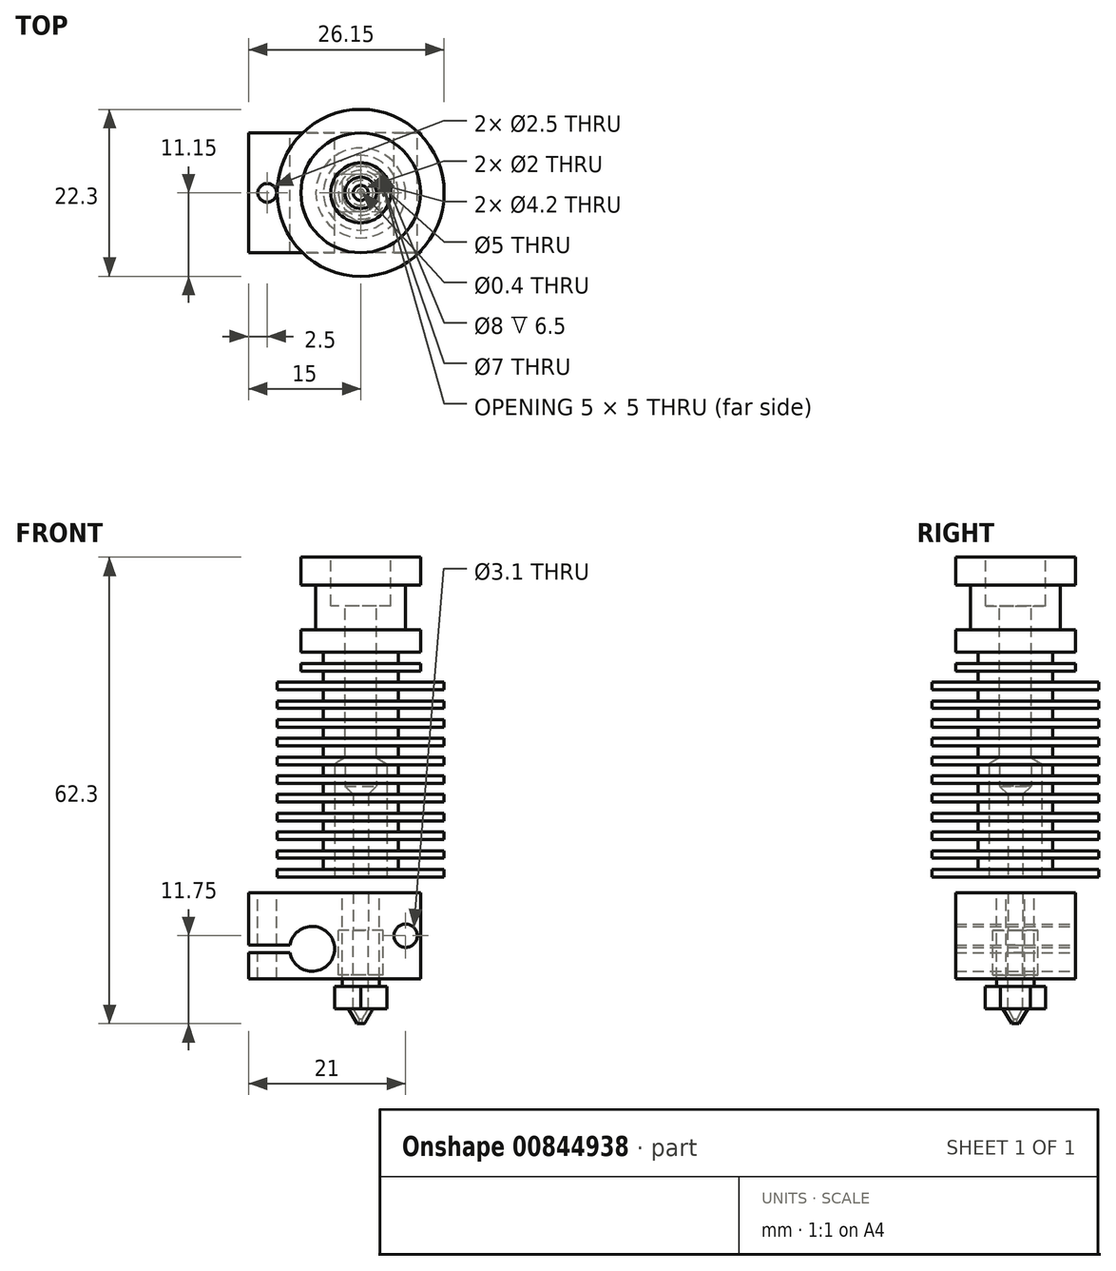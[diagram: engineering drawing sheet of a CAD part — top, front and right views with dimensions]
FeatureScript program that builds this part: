
annotation { "Feature Type Name" : "Feature", "Feature Type Description" : "" }
export const myFeature = defineFeature(function(context is Context, id is Id, definition is map)
    precondition{}
    {
        {
            var Q0;
            Q0=qCreatedBy(makeId("Front.planeOp"),FACE);
            var sketch = newSketch(context, id + "F0", { "sketchPlane" : qUnion([Q0])});
            skLineSegment(sketch, "E0.bottom", {"start": v(0, 0) * mm, "end": v(-8, 0) * mm});
            skLineSegment(sketch, "E0.top", {"start": v(0, 3.7) * mm, "end": v(-8, 3.7) * mm});
            skLineSegment(sketch, "E0.left", {"start": v(0, 0) * mm, "end": v(0, 3.7) * mm});
            skLineSegment(sketch, "E0.right", {"start": v(-8, 0) * mm, "end": v(-8, 3.7) * mm});
            skLineSegment(sketch, "E1.bottom", {"start": v(0, 0) * mm, "end": v(-6, 0) * mm});
            skLineSegment(sketch, "E1.top", {"start": v(0, -6) * mm, "end": v(-6, -6) * mm});
            skLineSegment(sketch, "E1.left", {"start": v(0, 0) * mm, "end": v(0, -6) * mm});
            skLineSegment(sketch, "E1.right", {"start": v(-6, 0) * mm, "end": v(-6, -6) * mm});
            skLineSegment(sketch, "E2.bottom", {"start": v(0, -6) * mm, "end": v(-8, -6) * mm});
            skLineSegment(sketch, "E2.top", {"start": v(0, -9) * mm, "end": v(-8, -9) * mm});
            skLineSegment(sketch, "E2.left", {"start": v(0, -6) * mm, "end": v(0, -9) * mm});
            skLineSegment(sketch, "E2.right", {"start": v(-8, -6) * mm, "end": v(-8, -9) * mm});
            skLineSegment(sketch, "E3.bottom", {"start": v(0, -9) * mm, "end": v(-5, -9) * mm});
            skLineSegment(sketch, "E3.top", {"start": v(0, -13) * mm, "end": v(-5, -13) * mm});
            skLineSegment(sketch, "E3.left", {"start": v(0, -9) * mm, "end": v(0, -13) * mm});
            skLineSegment(sketch, "E3.right", {"start": v(-5, -9) * mm, "end": v(-5, -13) * mm});
            skLineSegment(sketch, "E4.bottom", {"start": v(0, -13) * mm, "end": v(-11.15, -13) * mm});
            skLineSegment(sketch, "E4.top", {"start": v(0, -14) * mm, "end": v(-11.15, -14) * mm});
            skLineSegment(sketch, "E4.left", {"start": v(0, -13) * mm, "end": v(0, -14) * mm});
            skLineSegment(sketch, "E4.right", {"start": v(-11.15, -13) * mm, "end": v(-11.15, -14) * mm});
            skLineSegment(sketch, "E5.bottom", {"start": v(0, -14) * mm, "end": v(-5, -14) * mm});
            skLineSegment(sketch, "E5.top", {"start": v(0, -15.5) * mm, "end": v(-5, -15.5) * mm});
            skLineSegment(sketch, "E5.left", {"start": v(0, -14) * mm, "end": v(0, -15.5) * mm});
            skLineSegment(sketch, "E5.right", {"start": v(-5, -14) * mm, "end": v(-5, -15.5) * mm});
            skLineSegment(sketch, "E6.0.1.0", {"start": v(0, -16.5) * mm, "end": v(-11.15, -16.5) * mm});
            skLineSegment(sketch, "E6.0.1.1", {"start": v(-11.15, -15.5) * mm, "end": v(-11.15, -16.5) * mm});
            skLineSegment(sketch, "E6.0.1.2", {"start": v(0, -15.5) * mm, "end": v(-11.15, -15.5) * mm});
            skLineSegment(sketch, "E6.0.1.3", {"start": v(0, -15.5) * mm, "end": v(0, -16.5) * mm});
            skLineSegment(sketch, "E6.0.1.4", {"start": v(0, -16.5) * mm, "end": v(0, -18) * mm});
            skLineSegment(sketch, "E6.0.1.5", {"start": v(0, -18) * mm, "end": v(-5, -18) * mm});
            skLineSegment(sketch, "E6.0.1.6", {"start": v(-5, -16.5) * mm, "end": v(-5, -18) * mm});
            skLineSegment(sketch, "E6.0.2.0", {"start": v(0, -19) * mm, "end": v(-11.15, -19) * mm});
            skLineSegment(sketch, "E6.0.2.1", {"start": v(-11.15, -18) * mm, "end": v(-11.15, -19) * mm});
            skLineSegment(sketch, "E6.0.2.2", {"start": v(0, -18) * mm, "end": v(-11.15, -18) * mm});
            skLineSegment(sketch, "E6.0.2.3", {"start": v(0, -18) * mm, "end": v(0, -19) * mm});
            skLineSegment(sketch, "E6.0.2.4", {"start": v(0, -19) * mm, "end": v(0, -20.5) * mm});
            skLineSegment(sketch, "E6.0.2.5", {"start": v(0, -20.5) * mm, "end": v(-5, -20.5) * mm});
            skLineSegment(sketch, "E6.0.2.6", {"start": v(-5, -19) * mm, "end": v(-5, -20.5) * mm});
            skLineSegment(sketch, "E6.0.3.0", {"start": v(0, -21.5) * mm, "end": v(-11.15, -21.5) * mm});
            skLineSegment(sketch, "E6.0.3.1", {"start": v(-11.15, -20.5) * mm, "end": v(-11.15, -21.5) * mm});
            skLineSegment(sketch, "E6.0.3.2", {"start": v(0, -20.5) * mm, "end": v(-11.15, -20.5) * mm});
            skLineSegment(sketch, "E6.0.3.3", {"start": v(0, -20.5) * mm, "end": v(0, -21.5) * mm});
            skLineSegment(sketch, "E6.0.3.4", {"start": v(0, -21.5) * mm, "end": v(0, -23) * mm});
            skLineSegment(sketch, "E6.0.3.5", {"start": v(0, -23) * mm, "end": v(-5, -23) * mm});
            skLineSegment(sketch, "E6.0.3.6", {"start": v(-5, -21.5) * mm, "end": v(-5, -23) * mm});
            skLineSegment(sketch, "E6.0.4.0", {"start": v(0, -24) * mm, "end": v(-11.15, -24) * mm});
            skLineSegment(sketch, "E6.0.4.1", {"start": v(-11.15, -23) * mm, "end": v(-11.15, -24) * mm});
            skLineSegment(sketch, "E6.0.4.2", {"start": v(0, -23) * mm, "end": v(-11.15, -23) * mm});
            skLineSegment(sketch, "E6.0.4.3", {"start": v(0, -23) * mm, "end": v(0, -24) * mm});
            skLineSegment(sketch, "E6.0.4.4", {"start": v(0, -24) * mm, "end": v(0, -25.5) * mm});
            skLineSegment(sketch, "E6.0.4.5", {"start": v(0, -25.5) * mm, "end": v(-5, -25.5) * mm});
            skLineSegment(sketch, "E6.0.4.6", {"start": v(-5, -24) * mm, "end": v(-5, -25.5) * mm});
            skLineSegment(sketch, "E6.0.5.0", {"start": v(0, -26.5) * mm, "end": v(-11.15, -26.5) * mm});
            skLineSegment(sketch, "E6.0.5.1", {"start": v(-11.15, -25.5) * mm, "end": v(-11.15, -26.5) * mm});
            skLineSegment(sketch, "E6.0.5.2", {"start": v(0, -25.5) * mm, "end": v(-11.15, -25.5) * mm});
            skLineSegment(sketch, "E6.0.5.3", {"start": v(0, -25.5) * mm, "end": v(0, -26.5) * mm});
            skLineSegment(sketch, "E6.0.5.4", {"start": v(0, -26.5) * mm, "end": v(0, -28) * mm});
            skLineSegment(sketch, "E6.0.5.5", {"start": v(0, -28) * mm, "end": v(-5, -28) * mm});
            skLineSegment(sketch, "E6.0.5.6", {"start": v(-5, -26.5) * mm, "end": v(-5, -28) * mm});
            skLineSegment(sketch, "E6.0.6.0", {"start": v(0, -29) * mm, "end": v(-11.15, -29) * mm});
            skLineSegment(sketch, "E6.0.6.1", {"start": v(-11.15, -28) * mm, "end": v(-11.15, -29) * mm});
            skLineSegment(sketch, "E6.0.6.2", {"start": v(0, -28) * mm, "end": v(-11.15, -28) * mm});
            skLineSegment(sketch, "E6.0.6.3", {"start": v(0, -28) * mm, "end": v(0, -29) * mm});
            skLineSegment(sketch, "E6.0.6.4", {"start": v(0, -29) * mm, "end": v(0, -30.5) * mm});
            skLineSegment(sketch, "E6.0.6.5", {"start": v(0, -30.5) * mm, "end": v(-5, -30.5) * mm});
            skLineSegment(sketch, "E6.0.6.6", {"start": v(-5, -29) * mm, "end": v(-5, -30.5) * mm});
            skLineSegment(sketch, "E6.0.7.0", {"start": v(0, -31.5) * mm, "end": v(-11.15, -31.5) * mm});
            skLineSegment(sketch, "E6.0.7.1", {"start": v(-11.15, -30.5) * mm, "end": v(-11.15, -31.5) * mm});
            skLineSegment(sketch, "E6.0.7.2", {"start": v(0, -30.5) * mm, "end": v(-11.15, -30.5) * mm});
            skLineSegment(sketch, "E6.0.7.3", {"start": v(0, -30.5) * mm, "end": v(0, -31.5) * mm});
            skLineSegment(sketch, "E6.0.7.4", {"start": v(0, -31.5) * mm, "end": v(0, -33) * mm});
            skLineSegment(sketch, "E6.0.7.5", {"start": v(0, -33) * mm, "end": v(-5, -33) * mm});
            skLineSegment(sketch, "E6.0.7.6", {"start": v(-5, -31.5) * mm, "end": v(-5, -33) * mm});
            skLineSegment(sketch, "E6.0.8.0", {"start": v(0, -34) * mm, "end": v(-11.15, -34) * mm});
            skLineSegment(sketch, "E6.0.8.1", {"start": v(-11.15, -33) * mm, "end": v(-11.15, -34) * mm});
            skLineSegment(sketch, "E6.0.8.2", {"start": v(0, -33) * mm, "end": v(-11.15, -33) * mm});
            skLineSegment(sketch, "E6.0.8.3", {"start": v(0, -33) * mm, "end": v(0, -34) * mm});
            skLineSegment(sketch, "E6.0.8.4", {"start": v(0, -34) * mm, "end": v(0, -35.5) * mm});
            skLineSegment(sketch, "E6.0.8.5", {"start": v(0, -35.5) * mm, "end": v(-5, -35.5) * mm});
            skLineSegment(sketch, "E6.0.8.6", {"start": v(-5, -34) * mm, "end": v(-5, -35.5) * mm});
            skLineSegment(sketch, "E6.0.9.0", {"start": v(0, -36.5) * mm, "end": v(-11.15, -36.5) * mm});
            skLineSegment(sketch, "E6.0.9.1", {"start": v(-11.15, -35.5) * mm, "end": v(-11.15, -36.5) * mm});
            skLineSegment(sketch, "E6.0.9.2", {"start": v(0, -35.5) * mm, "end": v(-11.15, -35.5) * mm});
            skLineSegment(sketch, "E6.0.9.3", {"start": v(0, -35.5) * mm, "end": v(0, -36.5) * mm});
            skLineSegment(sketch, "E6.0.9.4", {"start": v(0, -36.5) * mm, "end": v(0, -38) * mm});
            skLineSegment(sketch, "E6.0.9.5", {"start": v(0, -38) * mm, "end": v(-5, -38) * mm});
            skLineSegment(sketch, "E6.0.9.6", {"start": v(-5, -36.5) * mm, "end": v(-5, -38) * mm});
            skLineSegment(sketch, "E6.direction1", {"start": v(-11.15, -14) * mm, "end": v(13.85, -14) * mm, "construction": true});
            skLineSegment(sketch, "E6.direction2", {"start": v(-11.15, -14) * mm, "end": v(-11.15, -16.5) * mm, "construction": true});
            skLineSegment(sketch, "E7.bottom", {"start": v(0, -38) * mm, "end": v(-11.15, -38) * mm});
            skLineSegment(sketch, "E7.top", {"start": v(0, -39) * mm, "end": v(-11.15, -39) * mm});
            skLineSegment(sketch, "E7.left", {"start": v(0, -38) * mm, "end": v(0, -39) * mm});
            skLineSegment(sketch, "E7.right", {"start": v(-11.15, -38) * mm, "end": v(-11.15, -39) * mm});
            skLineSegment(sketch, "E8", {"start": v(0, -13) * mm, "end": v(0, -11.5) * mm});
            skLineSegment(sketch, "E9.bottom", {"start": v(0, -11.5) * mm, "end": v(-8, -11.5) * mm});
            skLineSegment(sketch, "E9.top", {"start": v(0, -10.5) * mm, "end": v(-8, -10.5) * mm});
            skLineSegment(sketch, "E9.left", {"start": v(0, -11.5) * mm, "end": v(0, -10.5) * mm});
            skLineSegment(sketch, "E9.right", {"start": v(-8, -11.5) * mm, "end": v(-8, -10.5) * mm});
            skSolve(sketch);
        }
        {
            var Q0;
            Q0=makeQuery(id+"F0.imprint","IMPRINT",FACE,{"disambiguationData":[TD([[makeQuery(id+"F0.imprint","IMPRINT",EDGE,{"derivedFrom":sQuery(id+"F0.wireOp",EDGE,"E0.top")}),1.0]])]});
            var Q1;
            Q1=makeQuery(id+"F0.imprint","IMPRINT",FACE,{"disambiguationData":[TD([[makeQuery(id+"F0.imprint","IMPRINT",EDGE,{"derivedFrom":sQuery(id+"F0.wireOp",EDGE,"E1.top")}),-1.0]])]});
            var Q2;
            Q2=makeQuery(id+"F0.imprint","IMPRINT",FACE,{"disambiguationData":[TD([[makeQuery(id+"F0.imprint","IMPRINT",EDGE,{"derivedFrom":sQuery(id+"F0.wireOp",EDGE,"E3.top")}),1.0]])]});
            var Q3;
            {var subQ2=sQuery(id+"F0.wireOp",EDGE,"E6.0.6.4");Q3=makeQuery(id+"F0.imprint","IMPRINT",FACE,{"disambiguationData":[TD([[makeQuery(id+"F0.imprint","IMPRINT",EDGE,{"derivedFrom":subQ2}),-1.0]])]});}
            var Q4;
            {var subQ2=sQuery(id+"F0.wireOp",EDGE,"E6.0.5.4");Q4=makeQuery(id+"F0.imprint","IMPRINT",FACE,{"disambiguationData":[TD([[makeQuery(id+"F0.imprint","IMPRINT",EDGE,{"derivedFrom":subQ2}),-1.0]])]});}
            var Q5;
            Q5=makeQuery(id+"F0.imprint","IMPRINT",FACE,{"disambiguationData":[TD([[makeQuery(id+"F0.imprint","IMPRINT",EDGE,{"derivedFrom":sQuery(id+"F0.wireOp",EDGE,"E6.0.9.5")}),1.0]])]});
            var Q6;
            {var subQ1=sQuery(id+"F0.wireOp",EDGE,"E2.top");var subQ3=sQuery(id+"F0.wireOp",EDGE,"E3.right");var subQ4=makeQuery(id+"F0.imprint","INTERSECT",VERTEX,{"derivedFrom":[subQ1,subQ3]});Q6=makeQuery(id+"F0.imprint","IMPRINT",FACE,{"disambiguationData":[TD([[makeQuery(id+"F0.imprint","IMPRINT",EDGE,{"disambiguationData":[TD([[subQ4,-1.0]])],"derivedFrom":subQ3}),1.0]])]});}
            var Q7;
            {var subQ2=sQuery(id+"F0.wireOp",EDGE,"E6.0.7.4");Q7=makeQuery(id+"F0.imprint","IMPRINT",FACE,{"disambiguationData":[TD([[makeQuery(id+"F0.imprint","IMPRINT",EDGE,{"derivedFrom":subQ2}),-1.0]])]});}
            var Q8;
            {var subQ2=sQuery(id+"F0.wireOp",EDGE,"E6.0.2.4");Q8=makeQuery(id+"F0.imprint","IMPRINT",FACE,{"disambiguationData":[TD([[makeQuery(id+"F0.imprint","IMPRINT",EDGE,{"derivedFrom":subQ2}),-1.0]])]});}
            var Q9;
            {var subQ2=sQuery(id+"F0.wireOp",EDGE,"E6.0.3.4");Q9=makeQuery(id+"F0.imprint","IMPRINT",FACE,{"disambiguationData":[TD([[makeQuery(id+"F0.imprint","IMPRINT",EDGE,{"derivedFrom":subQ2}),-1.0]])]});}
            var Q10;
            Q10=makeQuery(id+"F0.imprint","IMPRINT",FACE,{"disambiguationData":[TD([[makeQuery(id+"F0.imprint","IMPRINT",EDGE,{"derivedFrom":sQuery(id+"F0.wireOp",EDGE,"E6.0.3.5")}),1.0]])]});
            var Q11;
            {var subQ2=sQuery(id+"F0.wireOp",EDGE,"E6.0.1.4");Q11=makeQuery(id+"F0.imprint","IMPRINT",FACE,{"disambiguationData":[TD([[makeQuery(id+"F0.imprint","IMPRINT",EDGE,{"derivedFrom":subQ2}),-1.0]])]});}
            var Q12;
            Q12=makeQuery(id+"F0.imprint","IMPRINT",FACE,{"disambiguationData":[TD([[makeQuery(id+"F0.imprint","IMPRINT",EDGE,{"derivedFrom":sQuery(id+"F0.wireOp",EDGE,"E6.0.7.5")}),1.0]])]});
            var Q13;
            {var subQ2=sQuery(id+"F0.wireOp",EDGE,"E6.0.4.4");Q13=makeQuery(id+"F0.imprint","IMPRINT",FACE,{"disambiguationData":[TD([[makeQuery(id+"F0.imprint","IMPRINT",EDGE,{"derivedFrom":subQ2}),-1.0]])]});}
            var Q14;
            {var subQ2=sQuery(id+"F0.wireOp",EDGE,"E6.0.8.4");Q14=makeQuery(id+"F0.imprint","IMPRINT",FACE,{"disambiguationData":[TD([[makeQuery(id+"F0.imprint","IMPRINT",EDGE,{"derivedFrom":subQ2}),-1.0]])]});}
            var Q15;
            Q15=makeQuery(id+"F0.imprint","IMPRINT",FACE,{"disambiguationData":[TD([[makeQuery(id+"F0.imprint","IMPRINT",EDGE,{"derivedFrom":sQuery(id+"F0.wireOp",EDGE,"E1.top")}),1.0]])]});
            var Q16;
            Q16=makeQuery(id+"F0.imprint","IMPRINT",FACE,{"disambiguationData":[TD([[makeQuery(id+"F0.imprint","IMPRINT",EDGE,{"derivedFrom":sQuery(id+"F0.wireOp",EDGE,"E6.0.8.5")}),1.0]])]});
            var Q17;
            {var subQ5=sQuery(id+"F0.wireOp",EDGE,"E9.right");Q17=makeQuery(id+"F0.imprint","IMPRINT",FACE,{"disambiguationData":[TD([[makeQuery(id+"F0.imprint","IMPRINT",EDGE,{"derivedFrom":subQ5}),-1.0]])]});}
            var Q18;
            Q18=makeQuery(id+"F0.imprint","IMPRINT",FACE,{"disambiguationData":[TD([[makeQuery(id+"F0.imprint","IMPRINT",EDGE,{"derivedFrom":sQuery(id+"F0.wireOp",EDGE,"E5.top")}),-1.0]])]});
            var Q19;
            {var subQ0=sQuery(id+"F0.wireOp",EDGE,"E3.top");Q19=makeQuery(id+"F0.imprint","IMPRINT",FACE,{"disambiguationData":[TD([[makeQuery(id+"F0.imprint","IMPRINT",EDGE,{"derivedFrom":subQ0}),-1.0]])]});}
            var Q20;
            Q20=makeQuery(id+"F0.imprint","IMPRINT",FACE,{"disambiguationData":[TD([[makeQuery(id+"F0.imprint","IMPRINT",EDGE,{"derivedFrom":sQuery(id+"F0.wireOp",EDGE,"E6.0.5.5")}),1.0]])]});
            var Q21;
            Q21=makeQuery(id+"F0.imprint","IMPRINT",FACE,{"disambiguationData":[TD([[makeQuery(id+"F0.imprint","IMPRINT",EDGE,{"derivedFrom":sQuery(id+"F0.wireOp",EDGE,"E6.0.6.5")}),1.0]])]});
            var Q22;
            {var subQ0=sQuery(id+"F0.wireOp",EDGE,"E9.bottom");var subQ1=sQuery(id+"F0.wireOp",EDGE,"E3.left");var subQ2=makeQuery(id+"F0.imprint","INTERSECT",VERTEX,{"derivedFrom":[subQ1,subQ0]});Q22=makeQuery(id+"F0.imprint","IMPRINT",FACE,{"disambiguationData":[TD([[makeQuery(id+"F0.imprint","IMPRINT",EDGE,{"disambiguationData":[TD([[subQ2,1.0]])],"derivedFrom":subQ1}),-1.0]])]});}
            var Q23;
            {var subQ2=sQuery(id+"F0.wireOp",EDGE,"E6.0.9.4");Q23=makeQuery(id+"F0.imprint","IMPRINT",FACE,{"disambiguationData":[TD([[makeQuery(id+"F0.imprint","IMPRINT",EDGE,{"derivedFrom":subQ2}),-1.0]])]});}
            var Q24;
            Q24=makeQuery(id+"F0.imprint","IMPRINT",FACE,{"disambiguationData":[TD([[makeQuery(id+"F0.imprint","IMPRINT",EDGE,{"derivedFrom":sQuery(id+"F0.wireOp",EDGE,"E6.0.4.5")}),1.0]])]});
            var Q25;
            Q25=makeQuery(id+"F0.imprint","IMPRINT",FACE,{"disambiguationData":[TD([[makeQuery(id+"F0.imprint","IMPRINT",EDGE,{"derivedFrom":sQuery(id+"F0.wireOp",EDGE,"E6.0.2.5")}),1.0]])]});
            var Q26;
            Q26=makeQuery(id+"F0.imprint","IMPRINT",FACE,{"disambiguationData":[TD([[makeQuery(id+"F0.imprint","IMPRINT",EDGE,{"derivedFrom":sQuery(id+"F0.wireOp",EDGE,"E6.0.1.5")}),1.0]])]});
            var Q27;
            Q27=makeQuery(id+"F0.imprint","IMPRINT",FACE,{"disambiguationData":[TD([[makeQuery(id+"F0.imprint","IMPRINT",EDGE,{"derivedFrom":sQuery(id+"F0.wireOp",EDGE,"E5.top")}),1.0]])]});
            var Q28;
            Q28=sQuery(id+"F0.wireOp",EDGE,"E1.left");
            revolve(context, id + "F1", {"surfaceOperationType" : NewSurfaceOperationType.NEW, "entities" : qUnion([Q0, Q1, Q2, Q3, Q4, Q5, Q6, Q7, Q8, Q9, Q10, Q11, Q12, Q13, Q14, Q15, Q16, Q17, Q18, Q19, Q20, Q21, Q22, Q23, Q24, Q25, Q26, Q27]), "axis" : qUnion([Q28]), "revolveType" : RevolveType.FULL});
        }
        {
            var Q0;
            Q0=makeQuery(id+"F1.opRevolve","SWEPT_FACE",FACE,{"disambiguationData":[OSD([sQuery(id+"F0.wireOp",EDGE,"E0.top")])]});
            var sketch = newSketch(context, id + "F2", { "sketchPlane" : qUnion([Q0])});
            skCircle(sketch, "E10", {"center": v(0, 0) * mm, "radius": 4 * mm});
            skSolve(sketch);
        }
        {
            var Q0;
            Q0=makeQuery(id+"F2.imprint","IMPRINT",FACE,{"disambiguationData":[TD([[makeQuery(id+"F2.imprint","IMPRINT",EDGE,{"derivedFrom":sQuery(id+"F2.wireOp",EDGE,"E10")}),1.0]])]});
            extrude(context, id + "F3", {"entities" : qUnion([Q0]), "operationType" : NewBodyOperationType.REMOVE, "oppositeDirection" : true, "depth" : 6.5 * mm, "offsetDistance" : 25 * mm});
        }
        {
            var Q0;
            Q0=makeQuery(id+"F3.boolean.opBoolean","COPY",FACE,{"derivedFrom":makeQuery(id+"F3.opExtrude","CAP_FACE",FACE,{"disambiguationData":[OSD([sQuery(id+"F2.wireOp",EDGE,"E10")])],"isStart":false})});
            var sketch = newSketch(context, id + "F4", { "sketchPlane" : qUnion([Q0])});
            skCircle(sketch, "E11", {"center": v(0, 0) * mm, "radius": 2.1 * mm});
            skSolve(sketch);
        }
        {
            var Q0;
            Q0=makeQuery(id+"F4.imprint","IMPRINT",FACE,{"disambiguationData":[TD([[makeQuery(id+"F4.imprint","IMPRINT",EDGE,{"derivedFrom":sQuery(id+"F4.wireOp",EDGE,"E11")}),1.0]])]});
            extrude(context, id + "F5", {"entities" : qUnion([Q0]), "operationType" : NewBodyOperationType.REMOVE, "oppositeDirection" : true, "depth" : 50 * mm, "offsetDistance" : 25 * mm});
        }
        {
            var Q0;
            Q0=makeQuery(id+"F1.opRevolve","SWEPT_FACE",FACE,{"disambiguationData":[OSD([sQuery(id+"F0.wireOp",EDGE,"E7.top")])]});
            var sketch = newSketch(context, id + "F6", { "sketchPlane" : qUnion([Q0])});
            skPoint(sketch, "E12", {"position": v(0, 0) * mm});
            skSolve(sketch);
        }
        {
            var Q0;
            Q0=sQuery(id+"F6.wireOp",VERTEX,"E12");
            var Q1;
            Q1=makeQuery(id+"F1.opRevolve","SWEPT_BODY",BODY,{"disambiguationData":[OSD([sQuery(id+"F0.wireOp",EDGE,"E0.bottom"),sQuery(id+"F0.wireOp",EDGE,"E0.top"),sQuery(id+"F0.wireOp",EDGE,"E0.left"),sQuery(id+"F0.wireOp",EDGE,"E0.right"),sQuery(id+"F0.wireOp",EDGE,"E1.left"),sQuery(id+"F0.wireOp",EDGE,"E1.right"),sQuery(id+"F0.wireOp",EDGE,"E2.bottom"),sQuery(id+"F0.wireOp",EDGE,"E2.top"),sQuery(id+"F0.wireOp",EDGE,"E2.left"),sQuery(id+"F0.wireOp",EDGE,"E2.right"),sQuery(id+"F0.wireOp",EDGE,"E3.left"),sQuery(id+"F0.wireOp",EDGE,"E3.right"),sQuery(id+"F0.wireOp",EDGE,"E4.bottom"),sQuery(id+"F0.wireOp",EDGE,"E4.top"),sQuery(id+"F0.wireOp",EDGE,"E4.left"),sQuery(id+"F0.wireOp",EDGE,"E4.right"),sQuery(id+"F0.wireOp",EDGE,"E5.left"),sQuery(id+"F0.wireOp",EDGE,"E5.right"),sQuery(id+"F0.wireOp",EDGE,"E6.0.1.0"),sQuery(id+"F0.wireOp",EDGE,"E6.0.1.1"),sQuery(id+"F0.wireOp",EDGE,"E6.0.1.2"),sQuery(id+"F0.wireOp",EDGE,"E6.0.1.3"),sQuery(id+"F0.wireOp",EDGE,"E6.0.1.4"),sQuery(id+"F0.wireOp",EDGE,"E6.0.1.6"),sQuery(id+"F0.wireOp",EDGE,"E6.0.2.0"),sQuery(id+"F0.wireOp",EDGE,"E6.0.2.1"),sQuery(id+"F0.wireOp",EDGE,"E6.0.2.2"),sQuery(id+"F0.wireOp",EDGE,"E6.0.2.3"),sQuery(id+"F0.wireOp",EDGE,"E6.0.2.4"),sQuery(id+"F0.wireOp",EDGE,"E6.0.2.6"),sQuery(id+"F0.wireOp",EDGE,"E6.0.3.0"),sQuery(id+"F0.wireOp",EDGE,"E6.0.3.1"),sQuery(id+"F0.wireOp",EDGE,"E6.0.3.2"),sQuery(id+"F0.wireOp",EDGE,"E6.0.3.3"),sQuery(id+"F0.wireOp",EDGE,"E6.0.3.4"),sQuery(id+"F0.wireOp",EDGE,"E6.0.3.6"),sQuery(id+"F0.wireOp",EDGE,"E6.0.4.0"),sQuery(id+"F0.wireOp",EDGE,"E6.0.4.1"),sQuery(id+"F0.wireOp",EDGE,"E6.0.4.2"),sQuery(id+"F0.wireOp",EDGE,"E6.0.4.3"),sQuery(id+"F0.wireOp",EDGE,"E6.0.4.4"),sQuery(id+"F0.wireOp",EDGE,"E6.0.4.6"),sQuery(id+"F0.wireOp",EDGE,"E6.0.5.0"),sQuery(id+"F0.wireOp",EDGE,"E6.0.5.1"),sQuery(id+"F0.wireOp",EDGE,"E6.0.5.2"),sQuery(id+"F0.wireOp",EDGE,"E6.0.5.3"),sQuery(id+"F0.wireOp",EDGE,"E6.0.5.4"),sQuery(id+"F0.wireOp",EDGE,"E6.0.5.6"),sQuery(id+"F0.wireOp",EDGE,"E6.0.6.0"),sQuery(id+"F0.wireOp",EDGE,"E6.0.6.1"),sQuery(id+"F0.wireOp",EDGE,"E6.0.6.2"),sQuery(id+"F0.wireOp",EDGE,"E6.0.6.3"),sQuery(id+"F0.wireOp",EDGE,"E6.0.6.4"),sQuery(id+"F0.wireOp",EDGE,"E6.0.6.6"),sQuery(id+"F0.wireOp",EDGE,"E6.0.7.0"),sQuery(id+"F0.wireOp",EDGE,"E6.0.7.1"),sQuery(id+"F0.wireOp",EDGE,"E6.0.7.2"),sQuery(id+"F0.wireOp",EDGE,"E6.0.7.3"),sQuery(id+"F0.wireOp",EDGE,"E6.0.7.4"),sQuery(id+"F0.wireOp",EDGE,"E6.0.7.6"),sQuery(id+"F0.wireOp",EDGE,"E6.0.8.0"),sQuery(id+"F0.wireOp",EDGE,"E6.0.8.1"),sQuery(id+"F0.wireOp",EDGE,"E6.0.8.2"),sQuery(id+"F0.wireOp",EDGE,"E6.0.8.3"),sQuery(id+"F0.wireOp",EDGE,"E6.0.8.4"),sQuery(id+"F0.wireOp",EDGE,"E6.0.8.6"),sQuery(id+"F0.wireOp",EDGE,"E6.0.9.0"),sQuery(id+"F0.wireOp",EDGE,"E6.0.9.1"),sQuery(id+"F0.wireOp",EDGE,"E6.0.9.2"),sQuery(id+"F0.wireOp",EDGE,"E6.0.9.3"),sQuery(id+"F0.wireOp",EDGE,"E6.0.9.4"),sQuery(id+"F0.wireOp",EDGE,"E6.0.9.6"),sQuery(id+"F0.wireOp",EDGE,"E7.bottom"),sQuery(id+"F0.wireOp",EDGE,"E7.top"),sQuery(id+"F0.wireOp",EDGE,"E7.left"),sQuery(id+"F0.wireOp",EDGE,"E7.right"),sQuery(id+"F0.wireOp",EDGE,"E9.bottom"),sQuery(id+"F0.wireOp",EDGE,"E9.top"),sQuery(id+"F0.wireOp",EDGE,"E9.right")])]});
            hole(context, id + "F7", {"style" : HoleStyle.SIMPLE, "endStyle" : HoleEndStyle.BLIND, "standardTappedOrClearance" : lookupTablePath({ "standard" : "ISO", "engagement" : "75%", "pitch" : "1 mm", "size" : "M8", "type" : "Tapped" }), "standardBlindInLast" : lookupTablePath({ "standard" : "ISO", "engagement" : "75%", "pitch" : "1 mm", "size" : "M8", "type" : "Tapped" }), "holeDiameter" : 7 * mm, "majorDiameter" : 8 * mm, "showTappedDepth" : true, "holeDepth" : 15.1 * mm, "isTappedThrough" : true, "tappedDepth" : 12.1 * mm, "tapClearance" : 3, "locations" : qUnion([Q0]), "scope" : qUnion([Q1])});
        }
        {
            var Q0;
            Q0=qCreatedBy(makeId("Front.planeOp"),FACE);
            var sketch = newSketch(context, id + "F8", { "sketchPlane" : qUnion([Q0])});
            skLineSegment(sketch, "E13", {"start": v(0, 0) * mm, "end": v(0, -39) * mm});
            skLineSegment(sketch, "E14", {"start": v(0, -39) * mm, "end": v(0, -24) * mm});
            skLineSegment(sketch, "E15.bottom", {"start": v(0, -39) * mm, "end": v(-3.5, -39) * mm});
            skLineSegment(sketch, "E15.top", {"start": v(0, -23.9) * mm, "end": v(-3.5, -23.9) * mm});
            skLineSegment(sketch, "E15.left", {"start": v(0, -39) * mm, "end": v(0, -23.9) * mm});
            skLineSegment(sketch, "E15.right", {"start": v(-3.5, -39) * mm, "end": v(-3.5, -23.9) * mm});
            skLineSegment(sketch, "E16", {"start": v(0, -23.9) * mm, "end": v(-2.1, -23.9) * mm});
            skLineSegment(sketch, "E17.bottom", {"start": v(0, -39) * mm, "end": v(-1, -39) * mm});
            skLineSegment(sketch, "E17.top", {"start": v(0, -26.9) * mm, "end": v(-1, -26.9) * mm});
            skLineSegment(sketch, "E17.left", {"start": v(0, -39) * mm, "end": v(0, -26.9) * mm});
            skLineSegment(sketch, "E17.right", {"start": v(-1, -39) * mm, "end": v(-1, -26.9) * mm});
            skLineSegment(sketch, "E18.bottom", {"start": v(-2.1, -23.9) * mm, "end": v(0, -23.9) * mm});
            skLineSegment(sketch, "E18.top", {"start": v(-2.1, -26.9) * mm, "end": v(0, -26.9) * mm});
            skLineSegment(sketch, "E18.left", {"start": v(-2.1, -23.9) * mm, "end": v(-2.1, -26.9) * mm});
            skLineSegment(sketch, "E18.right", {"start": v(0, -23.9) * mm, "end": v(0, -26.9) * mm});
            skLineSegment(sketch, "E19", {"start": v(-1, -26.9) * mm, "end": v(-1, -28) * mm});
            skLineSegment(sketch, "E20", {"start": v(-1, -28) * mm, "end": v(-2.1, -26.9) * mm});
            skLineSegment(sketch, "E21.bottom", {"start": v(0, -39) * mm, "end": v(-1.47, -39) * mm});
            skLineSegment(sketch, "E21.top", {"start": v(0, -41.1) * mm, "end": v(-1.47, -41.1) * mm});
            skLineSegment(sketch, "E21.left", {"start": v(0, -39) * mm, "end": v(0, -41.1) * mm});
            skLineSegment(sketch, "E21.right", {"start": v(-1.47, -39) * mm, "end": v(-1.47, -41.1) * mm});
            skLineSegment(sketch, "E22.bottom", {"start": v(-1, -39) * mm, "end": v(0, -39) * mm});
            skLineSegment(sketch, "E22.top", {"start": v(-1, -41.1) * mm, "end": v(0, -41.1) * mm});
            skLineSegment(sketch, "E22.left", {"start": v(-1, -39) * mm, "end": v(-1, -41.1) * mm});
            skLineSegment(sketch, "E23.bottom", {"start": v(0, -41.1) * mm, "end": v(-3, -41.1) * mm});
            skLineSegment(sketch, "E23.top", {"start": v(0, -46.1) * mm, "end": v(-3, -46.1) * mm});
            skLineSegment(sketch, "E23.left", {"start": v(0, -41.1) * mm, "end": v(0, -46.1) * mm});
            skLineSegment(sketch, "E23.right", {"start": v(-3, -41.1) * mm, "end": v(-3, -46.1) * mm});
            skLineSegment(sketch, "E24.top", {"start": v(-1, -46.1) * mm, "end": v(0, -46.1) * mm});
            skLineSegment(sketch, "E24.left", {"start": v(-1, -41.1) * mm, "end": v(-1, -46.1) * mm});
            skSolve(sketch);
        }
        {
            var Q0;
            Q0=makeQuery(id+"F8.imprint","IMPRINT",FACE,{"disambiguationData":[TD([[makeQuery(id+"F8.imprint","IMPRINT",EDGE,{"derivedFrom":sQuery(id+"F8.wireOp",EDGE,"E15.bottom")}),-1.0]])]});
            var Q1;
            Q1=makeQuery(id+"F8.imprint","IMPRINT",FACE,{"disambiguationData":[TD([[makeQuery(id+"F8.imprint","IMPRINT",EDGE,{"derivedFrom":sQuery(id+"F8.wireOp",EDGE,"E21.bottom")}),1.0]])]});
            var Q2;
            Q2=makeQuery(id+"F8.imprint","IMPRINT",FACE,{"disambiguationData":[TD([[makeQuery(id+"F8.imprint","IMPRINT",EDGE,{"derivedFrom":sQuery(id+"F8.wireOp",EDGE,"E23.top")}),-1.0]])]});
            var Q3;
            Q3=sQuery(id+"F8.wireOp",EDGE,"E14");
            revolve(context, id + "F9", {"surfaceOperationType" : NewSurfaceOperationType.NEW, "entities" : qUnion([Q0, Q1, Q2]), "axis" : qUnion([Q3]), "revolveType" : RevolveType.FULL});
        }
        {
            var Q0;
            Q0=qCreatedBy(makeId("Front.planeOp"),FACE);
            var sketch = newSketch(context, id + "F10", { "sketchPlane" : qUnion([Q0])});
            skLineSegment(sketch, "E25", {"start": v(0, 0) * mm, "end": v(0, -41.1) * mm});
            skLineSegment(sketch, "E26", {"start": v(0, -41.1) * mm, "end": v(8, -41.1) * mm});
            skLineSegment(sketch, "E27.bottom", {"start": v(8, -41.1) * mm, "end": v(-15, -41.1) * mm});
            skLineSegment(sketch, "E27.top", {"start": v(8, -52.6) * mm, "end": v(-15, -52.6) * mm});
            skLineSegment(sketch, "E27.left", {"start": v(8, -41.1) * mm, "end": v(8, -52.6) * mm});
            skLineSegment(sketch, "E27.right", {"start": v(-15, -41.1) * mm, "end": v(-15, -52.6) * mm});
            skLineSegment(sketch, "E28.bottom", {"start": v(8, -52.6) * mm, "end": v(-6.5, -52.6) * mm});
            skLineSegment(sketch, "E28.top", {"start": v(8, -48.6) * mm, "end": v(-6.5, -48.6) * mm});
            skLineSegment(sketch, "E28.left", {"start": v(8, -52.6) * mm, "end": v(8, -48.6) * mm});
            skLineSegment(sketch, "E28.right", {"start": v(-6.5, -52.6) * mm, "end": v(-6.5, -48.6) * mm});
            skCircle(sketch, "E29", {"center": v(-6.5, -48.6) * mm, "radius": 3 * mm});
            skLineSegment(sketch, "E30.bottom", {"start": v(8, -52.6) * mm, "end": v(6, -52.6) * mm});
            skLineSegment(sketch, "E30.top", {"start": v(8, -46.85) * mm, "end": v(6, -46.85) * mm});
            skLineSegment(sketch, "E30.left", {"start": v(8, -52.6) * mm, "end": v(8, -46.85) * mm});
            skLineSegment(sketch, "E30.right", {"start": v(6, -52.6) * mm, "end": v(6, -46.85) * mm});
            skCircle(sketch, "E31", {"center": v(6, -46.85) * mm, "radius": 1.55 * mm});
            skLineSegment(sketch, "E32", {"start": v(-6.5, -48.6) * mm, "end": v(-15, -48.6) * mm});
            skLineSegment(sketch, "E33.bottom", {"start": v(-5.23, -48.1) * mm, "end": v(-15.23, -48.1) * mm});
            skLineSegment(sketch, "E33.top", {"start": v(-5.23, -49.1) * mm, "end": v(-15.23, -49.1) * mm});
            skLineSegment(sketch, "E33.left", {"start": v(-5.23, -48.1) * mm, "end": v(-5.23, -49.1) * mm});
            skLineSegment(sketch, "E33.right", {"start": v(-15.23, -48.1) * mm, "end": v(-15.23, -49.1) * mm});
            skPoint(sketch, "E33.middle", {"position": v(-10.23, -48.6) * mm});
            skSolve(sketch);
        }
        {
            var Q0;
            {var subQ14=sQuery(id+"F10.wireOp",EDGE,"E26");Q0=makeQuery(id+"F10.imprint","IMPRINT",FACE,{"disambiguationData":[TD([[makeQuery(id+"F10.imprint","IMPRINT",EDGE,{"derivedFrom":subQ14}),-1.0]])]});}
            var Q1;
            {var subQ5=sQuery(id+"F10.wireOp",EDGE,"E27.top");var subQ7=sQuery(id+"F10.wireOp",EDGE,"E30.right");var subQ9=makeQuery(id+"F10.imprint","INTERSECT",VERTEX,{"derivedFrom":[subQ5,subQ7]});Q1=makeQuery(id+"F10.imprint","IMPRINT",FACE,{"disambiguationData":[TD([[makeQuery(id+"F10.imprint","IMPRINT",EDGE,{"disambiguationData":[TD([[subQ9,-1.0]])],"derivedFrom":subQ5}),-1.0]])]});}
            var Q2;
            {var subQ3=sQuery(id+"F10.wireOp",EDGE,"E27.top");var subQ5=sQuery(id+"F10.wireOp",EDGE,"E27.right");var subQ6=makeQuery(id+"F10.imprint","INTERSECT",VERTEX,{"derivedFrom":[subQ3,subQ5]});Q2=makeQuery(id+"F10.imprint","IMPRINT",FACE,{"disambiguationData":[TD([[makeQuery(id+"F10.imprint","IMPRINT",EDGE,{"disambiguationData":[TD([[subQ6,1.0]])],"derivedFrom":subQ3}),-1.0]])]});}
            var Q3;
            {var subQ0=sQuery(id+"F10.wireOp",EDGE,"E30.right");var subQ1=sQuery(id+"F10.wireOp",EDGE,"E27.top");var subQ2=makeQuery(id+"F10.imprint","INTERSECT",VERTEX,{"derivedFrom":[subQ1,subQ0]});Q3=makeQuery(id+"F10.imprint","IMPRINT",FACE,{"disambiguationData":[TD([[makeQuery(id+"F10.imprint","IMPRINT",EDGE,{"disambiguationData":[TD([[subQ2,1.0]])],"derivedFrom":subQ1}),-1.0]])]});}
            var Q4;
            {var subQ3=sQuery(id+"F10.wireOp",EDGE,"E27.left");var subQ6=sQuery(id+"F10.wireOp",EDGE,"E28.top");var subQ9=makeQuery(id+"F10.imprint","INTERSECT",VERTEX,{"derivedFrom":[subQ3,subQ6]});Q4=makeQuery(id+"F10.imprint","IMPRINT",FACE,{"disambiguationData":[TD([[makeQuery(id+"F10.imprint","IMPRINT",EDGE,{"disambiguationData":[TD([[subQ9,1.0]])],"derivedFrom":subQ3}),-1.0]])]});}
            extrude(context, id + "F11", {"entities" : qUnion([Q0, Q1, Q2, Q3, Q4]), "depth" : 16 * mm, "offsetDistance" : 25 * mm, "symmetric" : true});
        }
        {
            var Q0;
            Q0=makeQuery(id+"F11.opExtrude","SWEPT_FACE",FACE,{"disambiguationData":[OSD([sQuery(id+"F10.wireOp",EDGE,"E26"),sQuery(id+"F10.wireOp",EDGE,"E27.bottom")])]});
            var sketch = newSketch(context, id + "F12", { "sketchPlane" : qUnion([Q0])});
            skPoint(sketch, "E34", {"position": v(0, 0) * mm});
            skSolve(sketch);
        }
        {
            var Q0;
            Q0=sQuery(id+"F12.wireOp",VERTEX,"E34");
            var Q1;
            Q1=makeQuery(id+"F11.opExtrude","SWEPT_BODY",BODY,{"disambiguationData":[OSD([sQuery(id+"F10.wireOp",EDGE,"E26"),sQuery(id+"F10.wireOp",EDGE,"E27.bottom"),sQuery(id+"F10.wireOp",EDGE,"E27.top"),sQuery(id+"F10.wireOp",EDGE,"E27.left"),sQuery(id+"F10.wireOp",EDGE,"E27.right"),sQuery(id+"F10.wireOp",EDGE,"E29"),sQuery(id+"F10.wireOp",EDGE,"E31"),sQuery(id+"F10.wireOp",EDGE,"E33.bottom"),sQuery(id+"F10.wireOp",EDGE,"E33.top")])]});
            hole(context, id + "F13", {"style" : HoleStyle.SIMPLE, "endStyle" : HoleEndStyle.BLIND, "standardTappedOrClearance" : lookupTablePath({ "standard" : "ISO", "engagement" : "75%", "pitch" : "1 mm", "size" : "M6", "type" : "Tapped" }), "standardBlindInLast" : lookupTablePath({ "standard" : "ISO", "engagement" : "75%", "pitch" : "1 mm", "size" : "M6", "type" : "Tapped" }), "holeDiameter" : 5 * mm, "majorDiameter" : 6 * mm, "showTappedDepth" : true, "holeDepth" : 15.1 * mm, "isTappedThrough" : true, "tappedDepth" : 12.1 * mm, "tapClearance" : 3, "locations" : qUnion([Q0]), "scope" : qUnion([Q1])});
        }
        {
            var Q0;
            Q0=makeQuery(id+"F11.opExtrude","SWEPT_FACE",FACE,{"disambiguationData":[OSD([sQuery(id+"F10.wireOp",EDGE,"E26"),sQuery(id+"F10.wireOp",EDGE,"E27.bottom")])]});
            var sketch = newSketch(context, id + "F14", { "sketchPlane" : qUnion([Q0])});
            skLineSegment(sketch, "E35", {"start": v(8, 0) * mm, "end": v(-12.5, 0) * mm});
            skPoint(sketch, "E36", {"position": v(-12.5, 0) * mm});
            skSolve(sketch);
        }
        {
            var Q0;
            Q0=sQuery(id+"F14.wireOp",VERTEX,"E36");
            var Q1;
            Q1=makeQuery(id+"F11.opExtrude","SWEPT_BODY",BODY,{"disambiguationData":[OSD([sQuery(id+"F10.wireOp",EDGE,"E26"),sQuery(id+"F10.wireOp",EDGE,"E27.bottom"),sQuery(id+"F10.wireOp",EDGE,"E27.top"),sQuery(id+"F10.wireOp",EDGE,"E27.left"),sQuery(id+"F10.wireOp",EDGE,"E27.right"),sQuery(id+"F10.wireOp",EDGE,"E29"),sQuery(id+"F10.wireOp",EDGE,"E31"),sQuery(id+"F10.wireOp",EDGE,"E33.bottom"),sQuery(id+"F10.wireOp",EDGE,"E33.top")])]});
            hole(context, id + "F15", {"style" : HoleStyle.SIMPLE, "endStyle" : HoleEndStyle.BLIND, "standardTappedOrClearance" : lookupTablePath({ "standard" : "ISO", "engagement" : "75%", "pitch" : "0.5 mm", "size" : "M3", "type" : "Tapped" }), "standardBlindInLast" : lookupTablePath({ "standard" : "ISO", "engagement" : "75%", "pitch" : "0.5 mm", "size" : "M3", "type" : "Tapped" }), "holeDiameter" : 2.5 * mm, "majorDiameter" : 3 * mm, "showTappedDepth" : true, "holeDepth" : 21.5 * mm, "isTappedThrough" : true, "tappedDepth" : 20 * mm, "tapClearance" : 3, "locations" : qUnion([Q0]), "scope" : qUnion([Q1])});
        }
        {
            var Q0;
            Q0=qCreatedBy(makeId("Front.planeOp"),FACE);
            var sketch = newSketch(context, id + "F16", { "sketchPlane" : qUnion([Q0])});
            skLineSegment(sketch, "E37", {"start": v(0, 0) * mm, "end": v(0, -46.1) * mm});
            skLineSegment(sketch, "E38.bottom", {"start": v(0, -46.1) * mm, "end": v(-3, -46.1) * mm});
            skLineSegment(sketch, "E38.top", {"start": v(0, -53.6) * mm, "end": v(-3, -53.6) * mm});
            skLineSegment(sketch, "E38.left", {"start": v(0, -46.1) * mm, "end": v(0, -53.6) * mm});
            skLineSegment(sketch, "E38.right", {"start": v(-3, -46.1) * mm, "end": v(-3, -53.6) * mm});
            skLineSegment(sketch, "E39", {"start": v(0, -53.6) * mm, "end": v(0, -56.6) * mm});
            skLineSegment(sketch, "E40", {"start": v(0, -46.1) * mm, "end": v(0, -58.6) * mm});
            skLineSegment(sketch, "E41", {"start": v(0, -58.6) * mm, "end": v(-0.2, -58.6) * mm});
            skLineSegment(sketch, "E42", {"start": v(-0.2, -58.6) * mm, "end": v(-0.2, -58) * mm});
            skLineSegment(sketch, "E43.bottom", {"start": v(0, -53.6) * mm, "end": v(-2.5, -53.6) * mm});
            skLineSegment(sketch, "E43.top", {"start": v(0, -52.1) * mm, "end": v(-2.5, -52.1) * mm});
            skLineSegment(sketch, "E43.left", {"start": v(0, -53.6) * mm, "end": v(0, -52.1) * mm});
            skLineSegment(sketch, "E43.right", {"start": v(-2.5, -53.6) * mm, "end": v(-2.5, -52.1) * mm});
            skLineSegment(sketch, "E44", {"start": v(-2.5, -52.1) * mm, "end": v(-3, -52.1) * mm});
            skLineSegment(sketch, "E45", {"start": v(-0.2, -58) * mm, "end": v(-1, -56.61) * mm});
            skLineSegment(sketch, "E46", {"start": v(0, -56.6) * mm, "end": v(-1.65, -56.6) * mm});
            skLineSegment(sketch, "E47", {"start": v(-0.2, -58.6) * mm, "end": v(-0.5, -58.6) * mm});
            skLineSegment(sketch, "E48", {"start": v(-0.5, -58.6) * mm, "end": v(-1.65, -56.6) * mm});
            skLineSegment(sketch, "E49.bottom", {"start": v(0, -46.1) * mm, "end": v(-1, -46.1) * mm});
            skLineSegment(sketch, "E49.top", {"start": v(0, -56.6) * mm, "end": v(-1, -56.6) * mm});
            skLineSegment(sketch, "E49.left", {"start": v(0, -46.1) * mm, "end": v(0, -56.6) * mm});
            skLineSegment(sketch, "E49.right", {"start": v(-1, -46.1) * mm, "end": v(-1, -56.6) * mm});
            skLineSegment(sketch, "E50", {"start": v(-1, -56.6) * mm, "end": v(-1, -56.61) * mm});
            skLineSegment(sketch, "E51.bottom", {"start": v(-1, -56.6) * mm, "end": v(-2, -56.6) * mm});
            skLineSegment(sketch, "E51.top", {"start": v(-1, -53.6) * mm, "end": v(-2, -53.6) * mm});
            skLineSegment(sketch, "E51.left", {"start": v(-1, -56.6) * mm, "end": v(-1, -53.6) * mm});
            skLineSegment(sketch, "E51.right", {"start": v(-2, -56.6) * mm, "end": v(-2, -53.6) * mm});
            skSolve(sketch);
        }
        {
            var Q0;
            {var subQ0=sQuery(id+"F16.wireOp",EDGE,"E44");Q0=makeQuery(id+"F16.imprint","IMPRINT",FACE,{"disambiguationData":[TD([[makeQuery(id+"F16.imprint","IMPRINT",EDGE,{"derivedFrom":subQ0}),-1.0]])]});}
            var Q1;
            {var subQ0=sQuery(id+"F16.wireOp",EDGE,"E43.right");Q1=makeQuery(id+"F16.imprint","IMPRINT",FACE,{"disambiguationData":[TD([[makeQuery(id+"F16.imprint","IMPRINT",EDGE,{"derivedFrom":subQ0}),-1.0]])]});}
            var Q2;
            {var subQ6=sQuery(id+"F16.wireOp",EDGE,"E51.bottom");Q2=makeQuery(id+"F16.imprint","IMPRINT",FACE,{"disambiguationData":[TD([[makeQuery(id+"F16.imprint","IMPRINT",EDGE,{"derivedFrom":subQ6}),-1.0]])]});}
            var Q3;
            Q3=makeQuery(id+"F16.imprint","IMPRINT",FACE,{"disambiguationData":[TD([[makeQuery(id+"F16.imprint","IMPRINT",EDGE,{"derivedFrom":sQuery(id+"F16.wireOp",EDGE,"E42")}),1.0]])]});
            var Q4;
            Q4=sQuery(id+"F16.wireOp",EDGE,"E40");
            revolve(context, id + "F17", {"surfaceOperationType" : NewSurfaceOperationType.NEW, "entities" : qUnion([Q0, Q1, Q2, Q3]), "axis" : qUnion([Q4]), "revolveType" : RevolveType.FULL});
        }
        {
            var Q0;
            Q0=makeQuery(id+"F17.opRevolve","SWEPT_FACE",FACE,{"disambiguationData":[OSD([sQuery(id+"F16.wireOp",EDGE,"E38.top")])]});
            var sketch = newSketch(context, id + "F18", { "sketchPlane" : qUnion([Q0])});
            skCircle(sketch, "E52.cCircle", {"center": v(0, 0) * mm, "radius": 3.5 * mm, "construction": true});
            skLineSegment(sketch, "E52.0", {"start": v(3.5, 2.02) * mm, "end": v(3.5, -2.02) * mm});
            skLineSegment(sketch, "E52.1", {"start": v(3.5, -2.02) * mm, "end": v(0, -4.04) * mm});
            skLineSegment(sketch, "E52.2", {"start": v(0, -4.04) * mm, "end": v(-3.5, -2.02) * mm});
            skLineSegment(sketch, "E52.3", {"start": v(-3.5, -2.02) * mm, "end": v(-3.5, 2.02) * mm});
            skLineSegment(sketch, "E52.4", {"start": v(-3.5, 2.02) * mm, "end": v(0, 4.04) * mm});
            skLineSegment(sketch, "E52.5", {"start": v(0, 4.04) * mm, "end": v(3.5, 2.02) * mm});
            skPoint(sketch, "E52.0.midPoint", {"position": v(3.5, 0) * mm});
            skSolve(sketch);
        }
        {
            var Q0;
            Q0=makeQuery(id+"F18.imprint","IMPRINT",FACE,{"disambiguationData":[TD([[makeQuery(id+"F18.imprint","IMPRINT",EDGE,{"derivedFrom":sQuery(id+"F18.wireOp",EDGE,"E52.0")}),-1.0]])]});
            var Q1;
            {var subQ0=sQuery(id+"F16.wireOp",EDGE,"E38.top");Q1=makeQuery(id+"F18.imprint","IMPRINT",FACE,{"disambiguationData":[TD([[makeQuery(id+"F18.imprint","IMPRINT",EDGE,{"derivedFrom":makeQuery(id+"F17.opRevolve","SWEPT_EDGE",EDGE,{"disambiguationData":[OSD([subQ0,sQuery(id+"F16.wireOp",EDGE,"E43.right")])]})}),-1.0]])]});}
            extrude(context, id + "F19", {"entities" : qUnion([Q0, Q1]), "operationType" : NewBodyOperationType.ADD, "depth" : 3 * mm, "offsetDistance" : 25 * mm});
        }
    });
